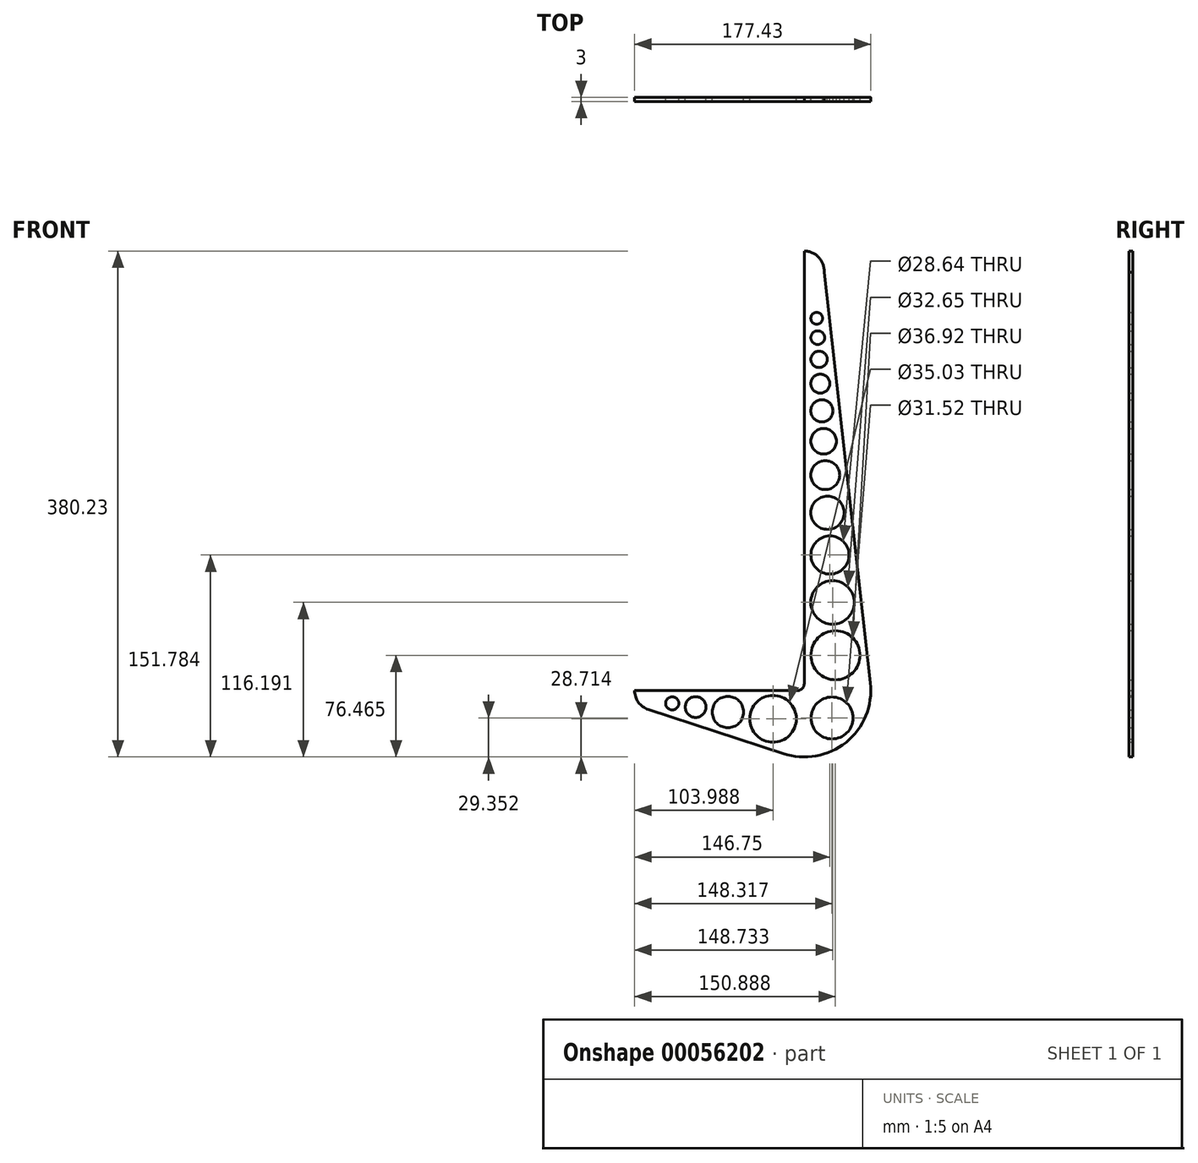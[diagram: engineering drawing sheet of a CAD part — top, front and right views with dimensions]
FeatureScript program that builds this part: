
annotation { "Feature Type Name" : "Feature", "Feature Type Description" : "" }
export const myFeature = defineFeature(function(context is Context, id is Id, definition is map)
    precondition{}
    {
        {
            var Q0;
            Q0=qCreatedBy(makeId("Front.planeOp"),FACE);
            var sketch = newSketch(context, id + "F0", { "sketchPlane" : qUnion([Q0])});
            skLineSegment(sketch, "E0", {"start": v(0, 5) * mm, "end": v(0, 330.23) * mm});
            skLineSegment(sketch, "E1", {"start": v(-5, 0) * mm, "end": v(-127.43, 0) * mm});
            skArc(sketch, "E2", {"start": v(-15.95, -47.39) * mm, "mid": v(31.4, -38.9) * mm, "end": v(49.69, 5.59) * mm});
            skArc(sketch, "E3", {"start": v(14.97, 314.22) * mm, "mid": v(10.96, 325.47) * mm, "end": v(0, 330.23) * mm});
            skArc(sketch, "E4", {"start": v(-127.43, 0) * mm, "mid": v(-124.58, -8.8) * mm, "end": v(-117.1, -14.25) * mm});
            skLineSegment(sketch, "E5", {"start": v(14.97, 314.22) * mm, "end": v(49.69, 5.59) * mm});
            skPoint(sketch, "E6.orphan", {"position": v(0, -52.76) * mm});
            skPoint(sketch, "E7.orphan", {"position": v(50.32, 0) * mm});
            skLineSegment(sketch, "E8", {"start": v(-15.95, -47.39) * mm, "end": v(-117.1, -14.25) * mm});
            skCircle(sketch, "E9", {"center": v(9.38, 279.7) * mm, "radius": 4.41 * mm});
            skCircle(sketch, "E10", {"center": v(10.14, 265.12) * mm, "radius": 5.18 * mm});
            skPoint(sketch, "E10.first.point", {"position": v(9.9, 270.3) * mm});
            skPoint(sketch, "E10.second.point", {"position": v(10.48, 259.95) * mm});
            skPoint(sketch, "E10.third.point", {"position": v(5, 264.52) * mm});
            skCircle(sketch, "E11", {"center": v(11.14, 248.83) * mm, "radius": 6.14 * mm});
            skPoint(sketch, "E11.first.point", {"position": v(10.76, 254.96) * mm});
            skPoint(sketch, "E11.second.point", {"position": v(11.45, 242.7) * mm});
            skPoint(sketch, "E11.third.point", {"position": v(5, 248.72) * mm});
            skCircle(sketch, "E12", {"center": v(12.12, 230.58) * mm, "radius": 7.13 * mm});
            skPoint(sketch, "E12.first.point", {"position": v(11.72, 237.7) * mm});
            skPoint(sketch, "E12.second.point", {"position": v(12.52, 223.46) * mm});
            skPoint(sketch, "E12.third.point", {"position": v(5, 230.1) * mm});
            skCircle(sketch, "E13", {"center": v(13.3, 210.17) * mm, "radius": 8.31 * mm});
            skPoint(sketch, "E13.first.point", {"position": v(12.8, 218.47) * mm});
            skPoint(sketch, "E13.second.point", {"position": v(13.73, 201.86) * mm});
            skPoint(sketch, "E13.third.point", {"position": v(5, 209.6) * mm});
            skCircle(sketch, "E14", {"center": v(14.59, 187.3) * mm, "radius": 9.59 * mm});
            skPoint(sketch, "E14.first.point", {"position": v(14, 196.87) * mm});
            skPoint(sketch, "E14.second.point", {"position": v(15.07, 177.73) * mm});
            skPoint(sketch, "E14.third.point", {"position": v(5, 187.22) * mm});
            skCircle(sketch, "E15", {"center": v(15.81, 161.89) * mm, "radius": 10.86 * mm});
            skPoint(sketch, "E15.first.point", {"position": v(15.35, 172.74) * mm});
            skPoint(sketch, "E15.second.point", {"position": v(16.56, 151.05) * mm});
            skPoint(sketch, "E15.third.point", {"position": v(5, 160.85) * mm});
            skCircle(sketch, "E16", {"center": v(17.5, 133.57) * mm, "radius": 12.51 * mm});
            skPoint(sketch, "E16.first.point", {"position": v(16.84, 146.06) * mm});
            skPoint(sketch, "E16.second.point", {"position": v(18.24, 121.08) * mm});
            skPoint(sketch, "E16.third.point", {"position": v(5, 133.92) * mm});
            skCircle(sketch, "E17", {"center": v(19.32, 101.78) * mm, "radius": 14.32 * mm});
            skPoint(sketch, "E17.first.point", {"position": v(18.52, 116.08) * mm});
            skPoint(sketch, "E17.second.point", {"position": v(20.11, 87.48) * mm});
            skPoint(sketch, "E17.third.point", {"position": v(5, 101.57) * mm});
            skCircle(sketch, "E18", {"center": v(21.3, 66.2) * mm, "radius": 16.33 * mm});
            skPoint(sketch, "E18.first.point", {"position": v(20.4, 82.5) * mm});
            skPoint(sketch, "E18.second.point", {"position": v(22.21, 49.9) * mm});
            skPoint(sketch, "E18.third.point", {"position": v(4.98, 65.73) * mm});
            skCircle(sketch, "E19", {"center": v(23.46, 26.47) * mm, "radius": 18.46 * mm});
            skPoint(sketch, "E19.first.point", {"position": v(22.5, 44.9) * mm});
            skPoint(sketch, "E19.second.point", {"position": v(24.55, 8.04) * mm});
            skPoint(sketch, "E19.third.point", {"position": v(5, 26.55) * mm});
            skCircle(sketch, "E20", {"center": v(-23.44, -21.29) * mm, "radius": 17.51 * mm});
            skPoint(sketch, "E20.first.point", {"position": v(-6.15, -24.05) * mm});
            skPoint(sketch, "E20.second.point", {"position": v(-40.76, -18.7) * mm});
            skPoint(sketch, "E20.third.point", {"position": v(-27.73, -38.27) * mm});
            skCircle(sketch, "E21", {"center": v(20.89, -20.65) * mm, "radius": 15.76 * mm});
            skPoint(sketch, "E21.second.point", {"position": v(11.98, -7.64) * mm});
            skPoint(sketch, "E21.third.point", {"position": v(28.32, -6.75) * mm});
            skCircle(sketch, "E22", {"center": v(-57.32, -16.21) * mm, "radius": 11.75 * mm});
            skPoint(sketch, "E22.first.point", {"position": v(-45.7, -17.93) * mm});
            skPoint(sketch, "E22.second.point", {"position": v(-68.92, -14.34) * mm});
            skPoint(sketch, "E22.third.point", {"position": v(-61.12, -27.33) * mm});
            skCircle(sketch, "E23", {"center": v(-81.58, -12.42) * mm, "radius": 7.8 * mm});
            skPoint(sketch, "E23.first.point", {"position": v(-73.86, -13.57) * mm});
            skPoint(sketch, "E23.second.point", {"position": v(-89.29, -11.19) * mm});
            skPoint(sketch, "E23.third.point", {"position": v(-84.33, -19.73) * mm});
            skCircle(sketch, "E24", {"center": v(-99.13, -9.68) * mm, "radius": 4.96 * mm});
            skPoint(sketch, "E24.first.point", {"position": v(-94.23, -10.42) * mm});
            skPoint(sketch, "E24.second.point", {"position": v(-104.02, -8.9) * mm});
            skPoint(sketch, "E24.third.point", {"position": v(-100.27, -14.5) * mm});
            skArc(sketch, "E25", {"start": v(-5, 0) * mm, "mid": v(-1.46, 1.46) * mm, "end": v(0, 5) * mm});
            skSolve(sketch);
        }
        {
            var Q0;
            Q0 = qSketchRegion(id + "F0", true);
            extrude(context, id + "F1", {"entities" : qUnion([Q0]), "depth" : 3 * mm});
        }
    });
